# Revit family: 23799-Deca_Bacia Basic Branco_Single_1198-13
name_source: partatom
category: Plumbing Fixtures
units: mm (PartAtom-declared; Revit-internal decimal feet)

## family parameters
Cut with Voids When Loaded = No
Host = Face
Part Type = Normal
Room Calculation Point = No
Round Connector Dimension = Use Radius
Shared = No

## types (1)
- 1198.C13_CROMADO
    Acompanha o Produto = Porca de fixação
    Aprovado por = quattroD
    Atendimento ao Cliente = 0800 011 7073
    CWFU = 0
    Categoria = METAIS PARA BANHEIRO
    Composição Anel Vedação = -
    Composição Assento = -
    Composição Básica = Liga de Cobre (bronze e latão),Liga de Zinco(zamac),Plásticos de Engenharia,Elastômeros
    Composição Componente = -
    Consumo = -
    Cor Interna = -
    Cor Principal = Cromado
    Cor Secundária = -
    Cores Componente = -
    Criado por = quattroD
    Código Pai = 1198.C13
    Default Elevation = 0 m
    Description = TORNEIRA P/ LAVATORIO MESA BICA ALTA DN15 GAMA -CROMADO
    Diâmetro Ponto de Esgoto = 0 m
    Diâmetro Água Fria = 0.02 m
    Informações Complementares = -
    Itens de Instalação = -
    Linha = Gama
    Manufacturer = Deca
    Material = Deca_Cromado
    Model = 1198.C13
    Norma = NBR 10281
    Peso Líquido (Kg) = 0.843
    Pressão mín. Aquec. Acúmulo = -
    Pressão mín. Aquec. Passagem = -
    Raio Ponto de Esgoto = 0 m
    Raio Água Fria = 0.01 m
    Saída de Esgoto = -
    Segmento = -
    Tipo de dispositivo economizador = RESTRITOR DECA COMFORT
    Tipo de mecanismo utilizado = MVC  - 1/4 de volta
    Tipo de rosca de entrada = BSP NBR 8133
    Tipo de rosca de saída = -
    URL = www.deca.com.br
    WFU = 0

## geometry (parser evidence)
native form markers: Sweep x2
no freeform markers — native parametric forms only
